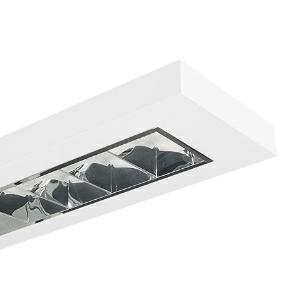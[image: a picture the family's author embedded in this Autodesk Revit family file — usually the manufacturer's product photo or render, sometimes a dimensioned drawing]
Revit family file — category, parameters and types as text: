
# Revit family: 3f_filippi_-_3f_travetta_2mg_3f_filippi_-_11484_-_3f_travetta_led_2x22w_dali_2mg_l1590
name_source: partatom
category: Lighting Fixtures
units: mm (PartAtom-declared; Revit-internal decimal feet)

## family parameters
Cut with Voids When Loaded = No
Host = Face
Light Source = No
Part Type = Normal
Room Calculation Point = No
Round Connector Dimension = Use Diameter
Shared = No

## types (1)
- 3F Filippi - 3F Travetta 2MG (1 x LED, 6236 lm, 49 W, 4000 K)
    Apparent Load = 49 VA
    Approval mark = ENEC
    CIE Flux Codes = 72 99 100 100 100
    Color Rendering = 80
    Color Temperature = 4000 K
    Control Gear = Electronic transformer
    Default Elevation = 1800 mm
    Description = ILLUMINOTECHNICAL
Luminous efficiency 100% (DLOR 100%, ULOR 0%).
Initial luminous flux of the luminaire 6236 lm.
Direct symmetric distribution.
Installation Interdistance Transv.D = 1.29 x hu - Long.D = 1.23 x hu.
Average luminance <1000 cd/m² for radial angles >65°.
Tabular UGR (CIE 117 - 4H-8H; S=0.25H; 70/50/20): RUG 17.1 - 19.3.
Beam angle: 80° - 84°.
Luminous efficacy 127 lm/W.
Lifetime (L93/B10): 30000 h. (tq+25°C)
Lifetime (L90/B10): 50000 h. (tq+25°C)
Lifetime (L85/B10): 80000 h. (tq+25°C)
Lifetime (L80/B10): 100000 h. (tq+25°C)
Sudden decreased luminous flux after 50000 hours: 0% (C0).
Photobiological safety in compliance with IEC/TR 62778: RG0 risk exempt, (IEC 62471).
In compliance with IEC/EN 62722-2-1 - IEC/EN 62717 standards.

SOURCE
2 linear LED modules 22W/840.
Energy efficiency class (UE 2019/2020 - UE 2019/2015): D.
CIE 13.3 Colour rendering index: CRI >80 (R9 <50%).
IES TM-30 Fidelity Index: Rf = 84 Rg = 95.
CCT nominal colour temperature 4000 K.
Colour initial tolerance (MacAdam): SDCM 2.

MECHANICAL
Housing with squared shape in white painted galvannealed steel, with nonreflecting surface.
2MG parabolic louvre, high efficiency, in specular aluminium with superficial titanium-magnesium treatment, non-iridescent, with transverse blades closed at the top.
Prismatic flat diffuser in transparent methacrylate (PMMA), multilenticular, anti-glare, prismatic exterior, placed above louvre blades.
Film protective against dust and finger marks, adhesive, attached to louvre.
Luminaire with limited surface temperature. - D - (EN 60598-2-24)
Dimensions: 1590x190 mm, height 60 mm (edge 40 mm). Weight 5.22 kg.
IP20 protection degree.
Mechanical strength to impacts IK02 (0.2 joule).
Glow-wire test resistance 650°C.

ELECTRICAL
Halogen Free DALI-2 DATI (Parts 251, 252, 253), PUSH-DIM, electronic wiring 230V-50/60Hz, power factor 0.95 at full load, THD <25%, constant output current, SELV, class I, 1 driver, 1 DALI addresse.
Power of the luminaire 49 W.
CE - IEC 60598-1 - EN 60598-1.
SAFE FLICKER: PstLM=<1 and SVM=<0.4 (IEC TR 61547-1 and IEC TR 63158), to ensure a more comfortable and safe light.
Luminaire compliant with EN 60598-2-22 for power supply from a centralised emergency system CPSS (Central Power Supply System), not incorporated in the luminaire - high risk areas excluded. The default power and flux are 100% in AC and 15% in DC.
Ambient temperature from 0°C to +25°C.
Temperature class T6 max 85°C.
5-pole terminal block for cascade line connection with connection capacity 2x2.5 mm².
Relative humidity UR: <85%.

INSTALLATION
Ceiling / Suspended.
All accessories dedicated to this product are available on the Catalog and on our website www.3F-Filippi.com.

APPLICATIONS
In environments, even with reduced height, requiring a comfortable light.
Exhibitions area, halls, great halls and shops.
In environments with VDTs, managerial offices and staterooms, public offices and schools.

LIGHT MANAGEMENT
Recommended minimum setting: 10%.
The luminaire, equipped with (DALI-2 DATI) driver, can be controlled manually with 3F Easy Dim technology or automatically/manually with wired or wireless DALI/D2D control systems.
The D2D driver guarantees interoperability with other devices with the same certification by making the following information available:
Device Data (Part 251), Energy Report (Part 252), Diagnosis & Maintenance (Part 253).
In electrical systems without a regulation system (manual or automatic) and DALI bus, a suitable jumper must be made on the DA-DA terminals of the appliance.

WARNING
Luminaire designed for disposal/recycling at end-of-life.
Replaceable (LED only) light source by a professional. Replaceable control gear by a professional.
    Height = 60 mm
    Lamp = 1 x LED
    Lamp Light Flux = 6236 lm
    Lamp Power = 49 W
    Lamp count = 1
    Length = 1590 mm
    Lifetime = 50000 h
    Luminous efficacy = 127 lm/W
    Manufacturer = 3F Filippi
    ModVariant = No
    Model = 3F Filippi - 11484 - 3F Travetta LED 2x22W DALI 2MG L1590
    Mounting Place = Ceiling
    Mounting Type = Pendant
    Number of Poles = 1
    OnlyDefault = Yes
    Power Factor = 1
    Product Name = 3F Filippi - 3F Travetta 2MG
    Product group = pendant luminaire
    ProductGroupID = 9
    Protection Class = Protection class I
    Protection Degree = IP 20
    RLX_Detail_Level = 1
    RLX_Emergency_Light_Flux = 0 lm
    RLX_Emergency_Type = 0
    RLX_Emergency_Type_DB = No
    RlxData = <blob elided: 57589 chars, md5=693f01c5>
    Socket = socket
    Standby Power = 0 W
    System Light Flux = 6236 lm
    System Power = 49 W
    Type Comments = Product without accessories
    Type Image = 3ffilippi_3f_travetta_led_2mg.jpg
    URL = http://relux.com
    VarID = ---
    Voltage = 0 V
    Weight = 0.00 kg
    Width = 190 mm

## geometry (parser evidence)
native form markers: Blend x4, Sweep x9
no freeform markers — native parametric forms only
